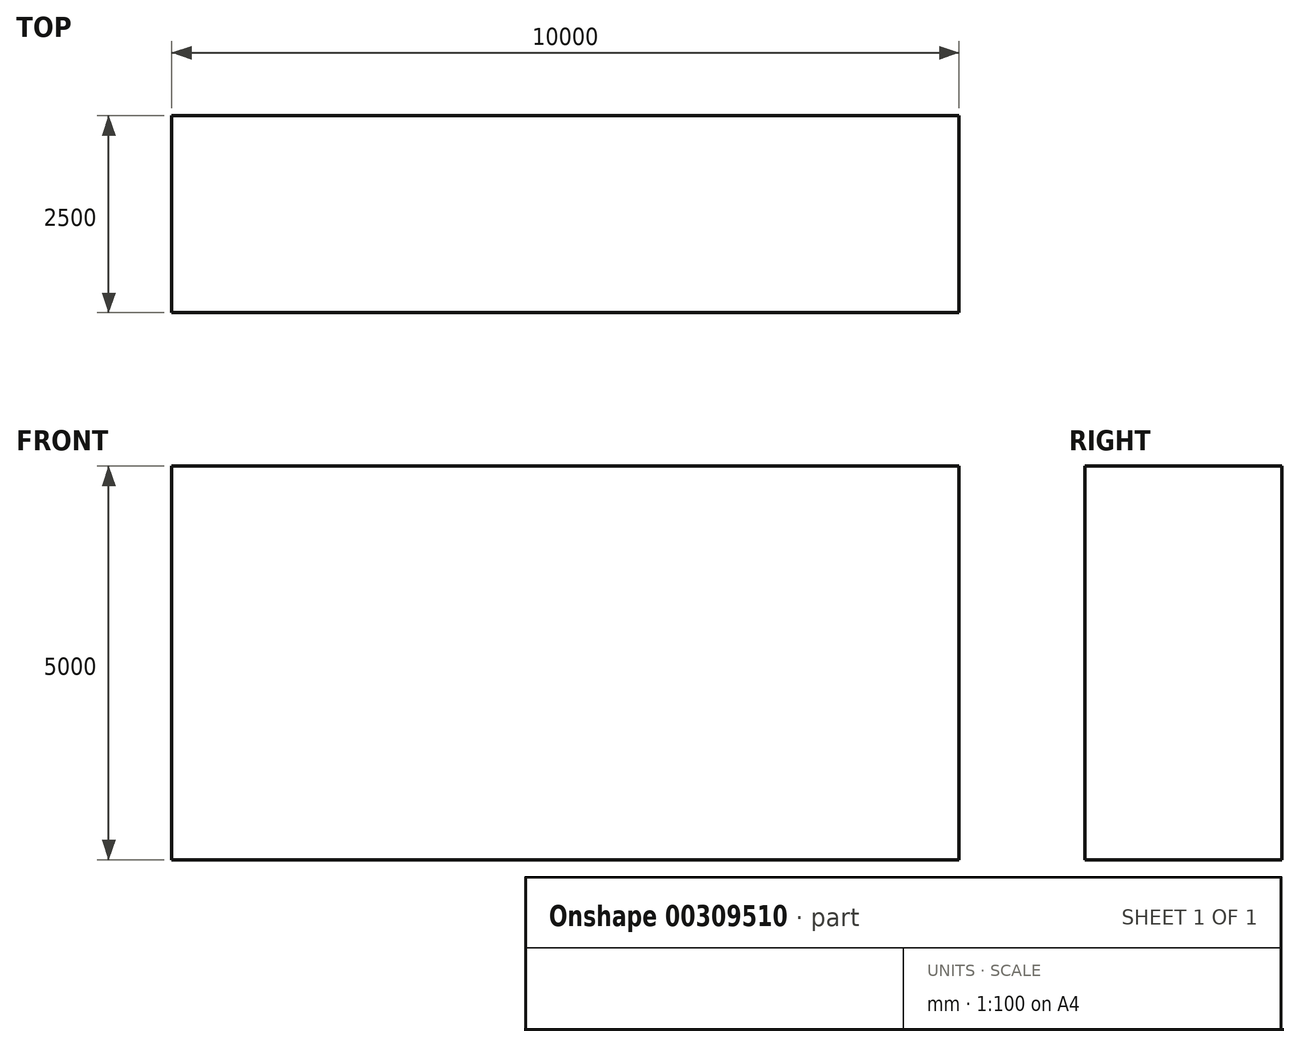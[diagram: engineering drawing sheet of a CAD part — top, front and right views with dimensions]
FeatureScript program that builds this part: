
annotation { "Feature Type Name" : "Feature", "Feature Type Description" : "" }
export const myFeature = defineFeature(function(context is Context, id is Id, definition is map)
    precondition{}
    {
        {
            var Q0;
            Q0=qCreatedBy(makeId("Front.planeOp"),FACE);
            var sketch = newSketch(context, id + "F0", { "sketchPlane" : qUnion([Q0])});
            skLineSegment(sketch, "E0.bottom", {"start": v(0, 0) * mm, "end": v(10000, 0) * mm});
            skLineSegment(sketch, "E0.top", {"start": v(0, -5000) * mm, "end": v(10000, -5000) * mm});
            skLineSegment(sketch, "E0.left", {"start": v(0, 0) * mm, "end": v(0, -5000) * mm});
            skLineSegment(sketch, "E0.right", {"start": v(10000, 0) * mm, "end": v(10000, -5000) * mm});
            skSolve(sketch);
        }
        {
            var Q0;
            Q0 = qSketchRegion(id + "F0", true);
            extrude(context, id + "F1", {"entities" : qUnion([Q0]), "depth" : 2500 * mm});
        }
    });
